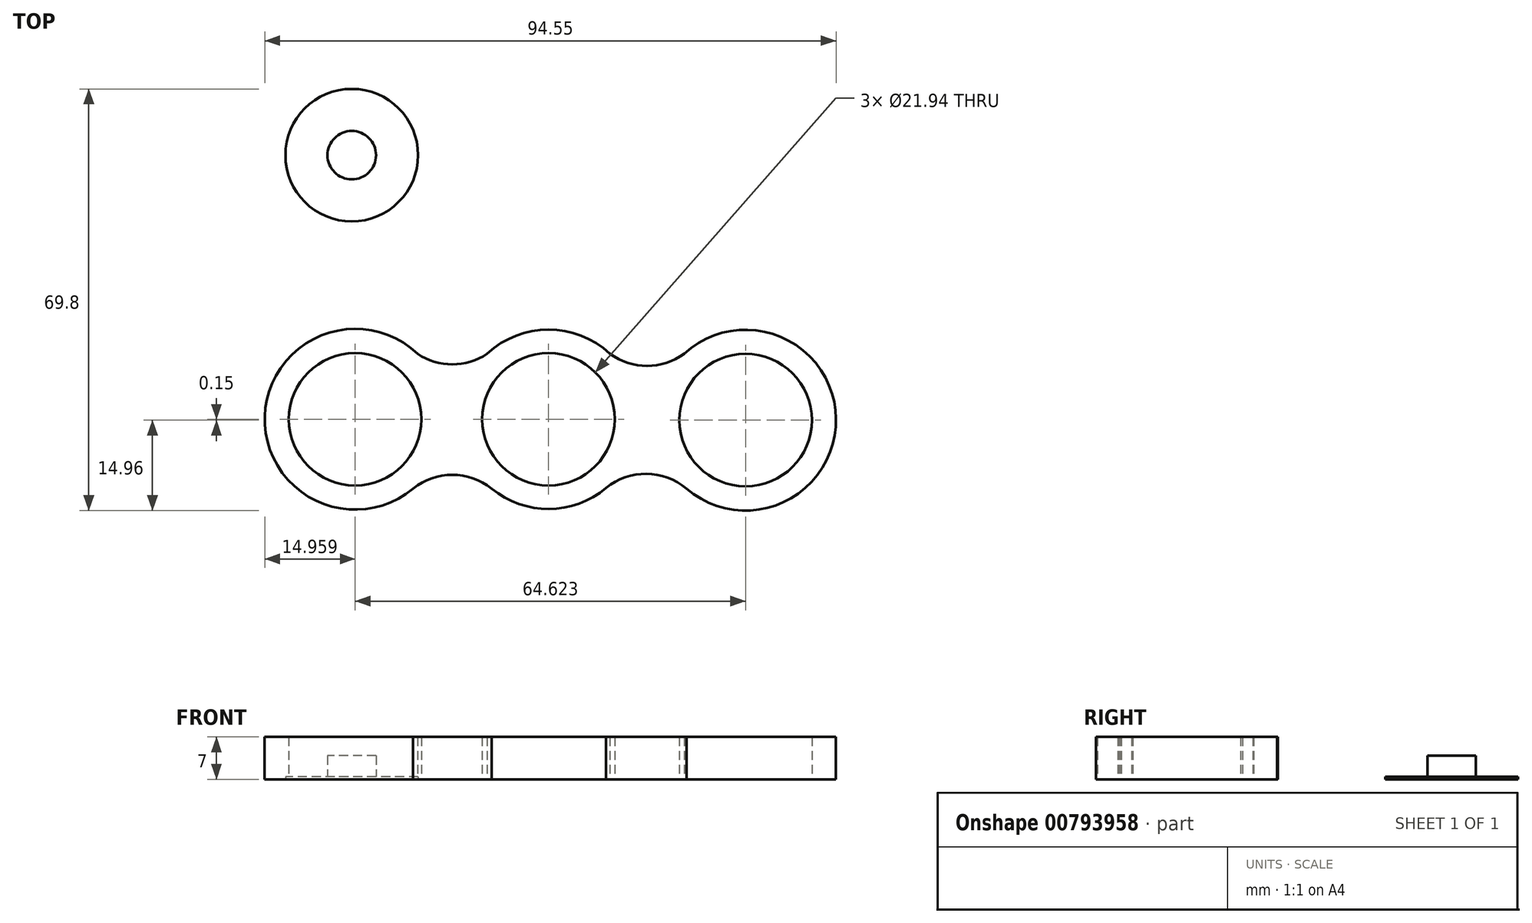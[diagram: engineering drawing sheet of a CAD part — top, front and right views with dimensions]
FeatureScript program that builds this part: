
annotation { "Feature Type Name" : "Feature", "Feature Type Description" : "" }
export const myFeature = defineFeature(function(context is Context, id is Id, definition is map)
    precondition{}
    {
        {
            var Q0;
            Q0=qCreatedBy(makeId("Top.planeOp"),FACE);
            var sketch = newSketch(context, id + "F0", { "sketchPlane" : qUnion([Q0])});
            skCircle(sketch, "E0", {"center": v(0, 0) * mm, "radius": 10.97 * mm});
            skCircle(sketch, "E1", {"center": v(0, 0) * mm, "radius": 14.85 * mm});
            skCircle(sketch, "E2", {"center": v(-32.01, 0) * mm, "radius": 10.97 * mm});
            skCircle(sketch, "E3", {"center": v(32.61, -0.15) * mm, "radius": 10.97 * mm});
            skCircle(sketch, "E4", {"center": v(32.61, -0.15) * mm, "radius": 14.96 * mm});
            skCircle(sketch, "E5", {"center": v(-32.01, 0) * mm, "radius": 14.96 * mm});
            skPoint(sketch, "E6", {"position": v(9.42, -11.48) * mm});
            skPoint(sketch, "E7", {"position": v(22.46, 10.84) * mm});
            skPoint(sketch, "E8", {"position": v(10.15, 10.84) * mm});
            skPoint(sketch, "E9", {"position": v(22.84, -11.48) * mm});
            skPoint(sketch, "E10", {"position": v(-10.15, 10.84) * mm});
            skPoint(sketch, "E11", {"position": v(-21.7, 10.84) * mm});
            skPoint(sketch, "E12", {"position": v(-9.42, -11.48) * mm});
            skPoint(sketch, "E13", {"position": v(-22.41, -11.48) * mm});
            skArc(sketch, "E14", {"start": v(-21.7, 10.84) * mm, "mid": v(-15.93, 9.1) * mm, "end": v(-10.15, 10.84) * mm});
            skArc(sketch, "E15", {"start": v(10.15, 10.84) * mm, "mid": v(16.3, 8.83) * mm, "end": v(22.46, 10.84) * mm});
            skArc(sketch, "E16", {"start": v(-9.42, -11.48) * mm, "mid": v(-15.92, -9.21) * mm, "end": v(-22.41, -11.48) * mm});
            skArc(sketch, "E17", {"start": v(22.84, -11.48) * mm, "mid": v(16.13, -9.04) * mm, "end": v(9.42, -11.48) * mm});
            skSolve(sketch);
        }
        {
            var Q0;
            Q0=qSketchRegion(id+"F0",true);
            extrude(context, id + "F1", {"entities" : qUnion([Q0]), "depth" : 7 * mm, "offsetDistance" : 25 * mm});
        }
        {
            var Q0;
            Q0=qCreatedBy(makeId("Top.planeOp"),FACE);
            var sketch = newSketch(context, id + "F2", { "sketchPlane" : qUnion([Q0])});
            skCircle(sketch, "E18", {"center": v(-32.57, 43.72) * mm, "radius": 10.97 * mm});
            skCircle(sketch, "E19", {"center": v(-32.57, 43.72) * mm, "radius": 4 * mm});
            skCircle(sketch, "E20", {"center": v(20.3, 44) * mm, "radius": 4 * mm});
            skCircle(sketch, "E21", {"center": v(20.3, 44) * mm, "radius": 10.97 * mm});
            skSolve(sketch);
        }
        {
            var Q0;
            Q0=makeQuery(id+"F2.imprint","IMPRINT",FACE,{"disambiguationData":[TD([[makeQuery(id+"F2.imprint","IMPRINT",EDGE,{"derivedFrom":sQuery(id+"F2.wireOp",EDGE,"E18")}),1.0]])]});
            extrude(context, id + "F3", {"entities" : qUnion([Q0]), "depth" : 0.4 * mm, "offsetDistance" : 25 * mm});
        }
        {
            var Q0;
            Q0=makeQuery(id+"F2.imprint","IMPRINT",FACE,{"disambiguationData":[TD([[makeQuery(id+"F2.imprint","IMPRINT",EDGE,{"derivedFrom":sQuery(id+"F2.wireOp",EDGE,"E19")}),1.0]])]});
            extrude(context, id + "F4", {"entities" : qUnion([Q0]), "operationType" : NewBodyOperationType.ADD, "depth" : 3.9 * mm, "offsetDistance" : 25 * mm});
        }
    });
